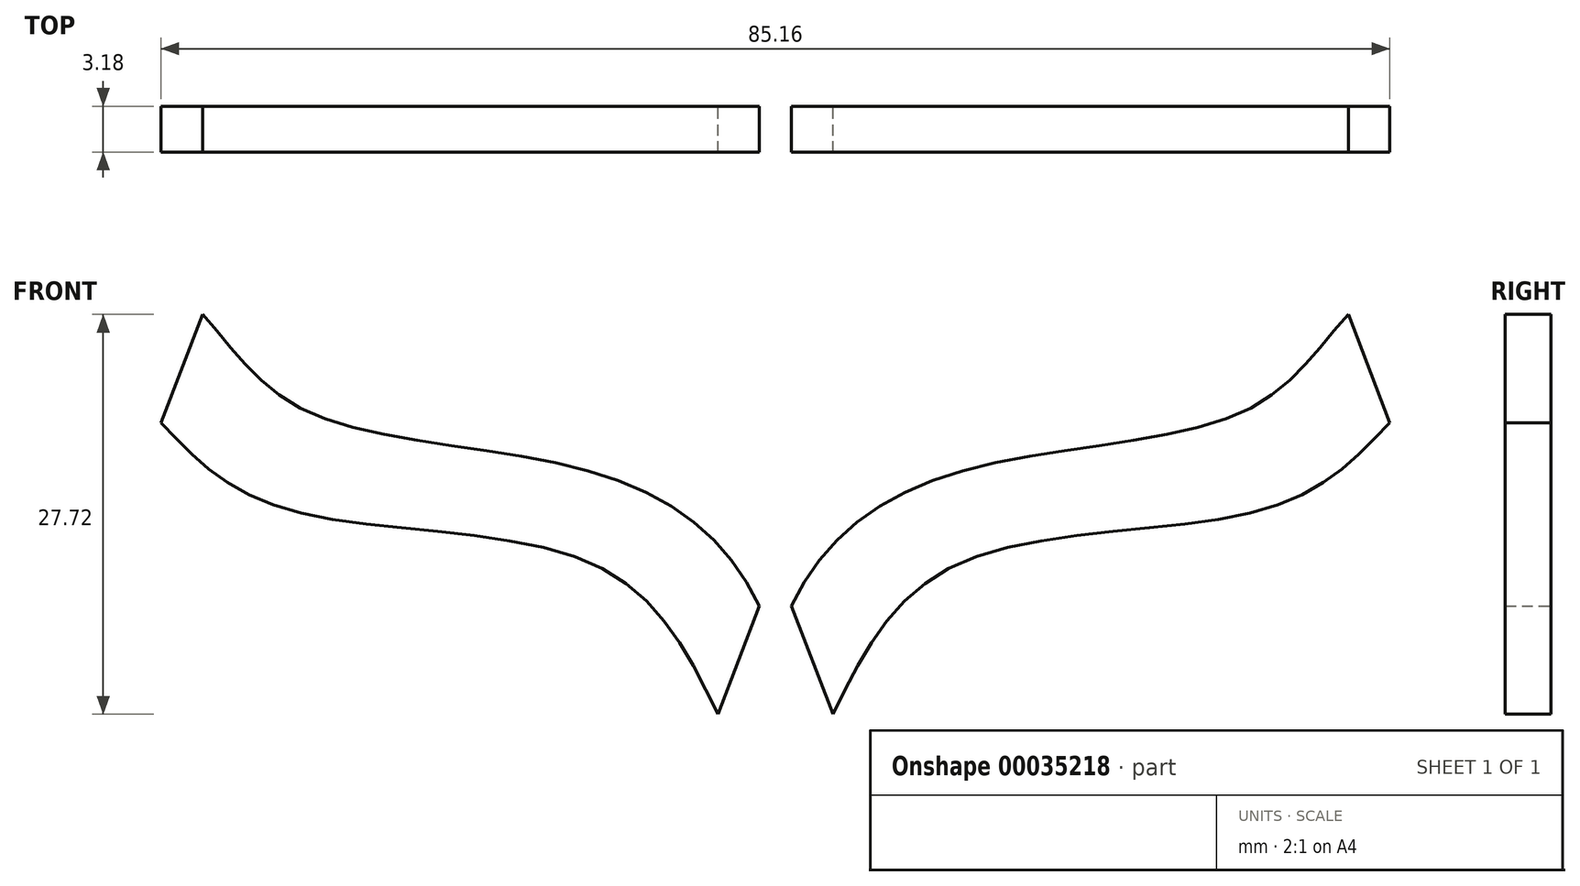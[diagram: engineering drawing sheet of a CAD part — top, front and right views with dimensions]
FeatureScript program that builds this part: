
annotation { "Feature Type Name" : "Feature", "Feature Type Description" : "" }
export const myFeature = defineFeature(function(context is Context, id is Id, definition is map)
    precondition{}
    {
        {
            var Q0;
            Q0=qCreatedBy(makeId("Front.planeOp"),FACE);
            var sketch = newSketch(context, id + "F0", { "sketchPlane" : qUnion([Q0])});
            skFitSpline(sketch, "E0", {"points": [v(3.99, 0.98) * mm, v(12.53, 11.35) * mm, v(34.04, 15.23) * mm, v(42.58, 21.2) * mm], "startDerivative": vector(19.1, 39.07) * mm, "endDerivative": vector(23.97, 25.4) * mm});
            skFitSpline(sketch, "E1.MirrorCS", {"points": [v(-3.99, 0.98) * mm, v(-12.53, 11.35) * mm, v(-34.04, 15.23) * mm, v(-42.58, 21.2) * mm], "startDerivative": vector(-19.1, 39.07) * mm, "endDerivative": vector(-23.97, 25.4) * mm});
            skFitSpline(sketch, "E2", {"points": [v(1.1, 8.5) * mm, v(11.99, 17.56) * mm, v(32.45, 21.97) * mm, v(39.7, 28.7) * mm], "startDerivative": vector(18.47, 39.37) * mm, "endDerivative": vector(23.56, 25.79) * mm});
            skLineSegment(sketch, "E3", {"start": v(42.58, 21.2) * mm, "end": v(39.7, 28.7) * mm});
            skLineSegment(sketch, "E4", {"start": v(3.99, 0.98) * mm, "end": v(1.1, 8.5) * mm});
            skFitSpline(sketch, "E5.MirrorCS", {"points": [v(-1.1, 8.5) * mm, v(-11.99, 17.56) * mm, v(-32.45, 21.97) * mm, v(-39.7, 28.7) * mm], "startDerivative": vector(-18.47, 39.37) * mm, "endDerivative": vector(-23.56, 25.79) * mm});
            skLineSegment(sketch, "E6", {"start": v(-3.99, 0.98) * mm, "end": v(-1.1, 8.5) * mm});
            skLineSegment(sketch, "E7", {"start": v(-42.58, 21.2) * mm, "end": v(-39.7, 28.7) * mm});
            skSolve(sketch);
        }
        {
            var Q0;
            Q0=makeQuery(id+"F0.imprint","IMPRINT",FACE,{"disambiguationData":[TD([[makeQuery(id+"F0.imprint","IMPRINT",EDGE,{"derivedFrom":sQuery(id+"F0.wireOp",EDGE,"E1.MirrorCS")}),-1.0]])]});
            var Q1;
            Q1=makeQuery(id+"F0.imprint","IMPRINT",FACE,{"disambiguationData":[TD([[makeQuery(id+"F0.imprint","IMPRINT",EDGE,{"derivedFrom":sQuery(id+"F0.wireOp",EDGE,"E0")}),1.0]])]});
            extrude(context, id + "F1", {"entities" : qUnion([Q0, Q1]), "depth" : 3.17 * mm});
        }
    });
